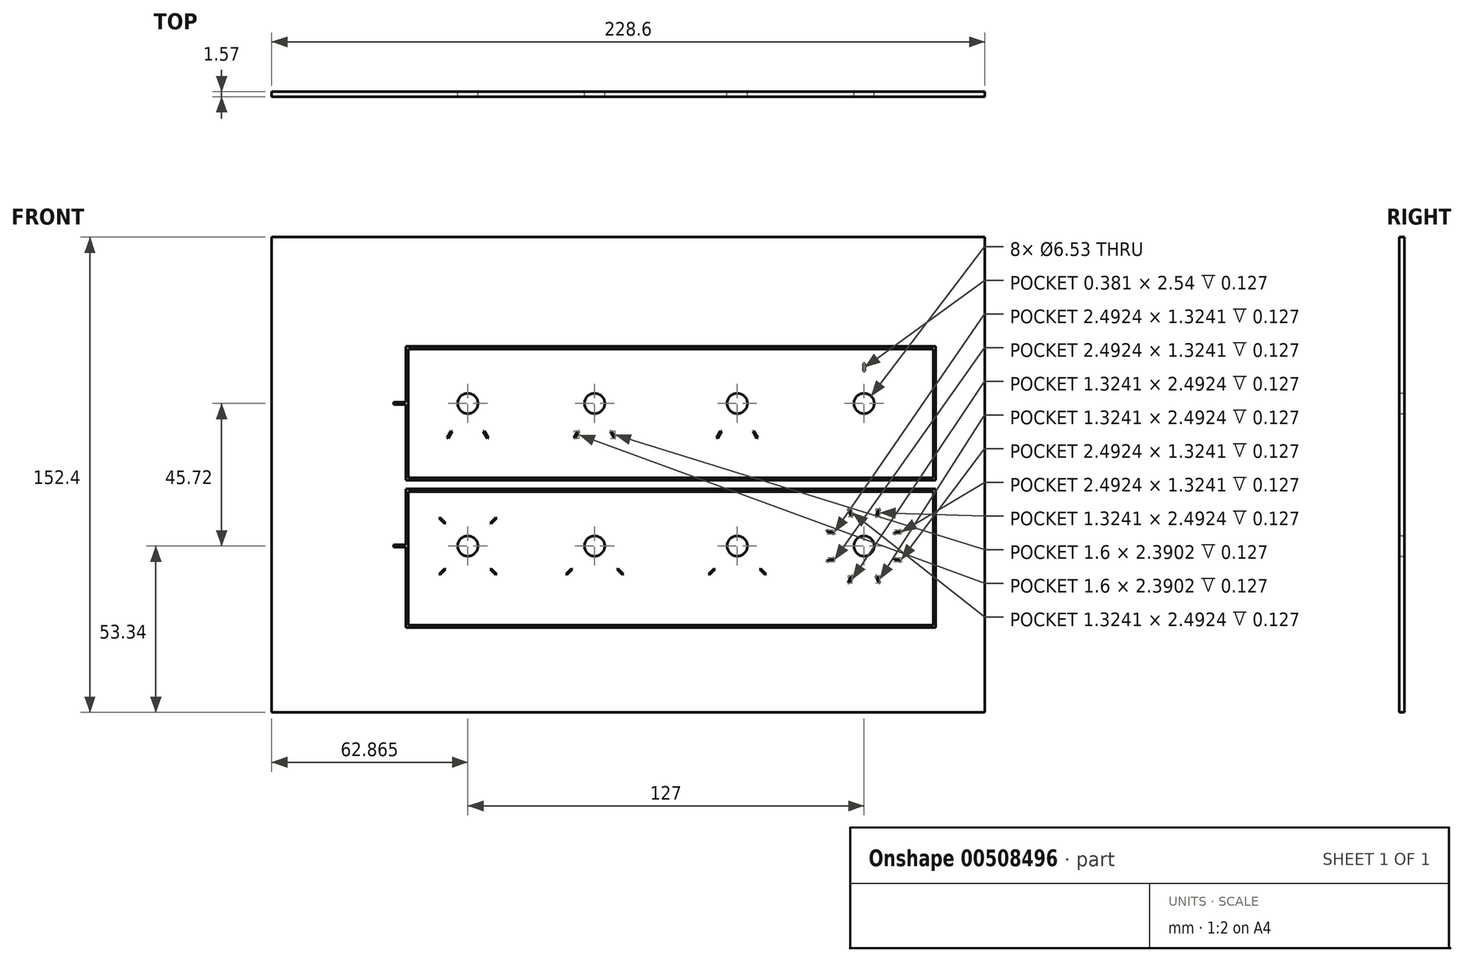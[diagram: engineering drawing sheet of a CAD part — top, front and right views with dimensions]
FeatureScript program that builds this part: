
annotation { "Feature Type Name" : "Feature", "Feature Type Description" : "" }
export const myFeature = defineFeature(function(context is Context, id is Id, definition is map)
    precondition{}
    {
        {
            var Q0;
            Q0=qCreatedBy(makeId("Front.planeOp"),FACE);
            var sketch = newSketch(context, id + "F0", { "sketchPlane" : qUnion([Q0])});
            skLineSegment(sketch, "E0.bottom", {"start": v(114.3, -76.2) * mm, "end": v(-114.3, -76.2) * mm});
            skLineSegment(sketch, "E0.top", {"start": v(114.3, 76.2) * mm, "end": v(-114.3, 76.2) * mm});
            skLineSegment(sketch, "E0.left", {"start": v(114.3, -76.2) * mm, "end": v(114.3, 76.2) * mm});
            skLineSegment(sketch, "E0.right", {"start": v(-114.3, -76.2) * mm, "end": v(-114.3, 76.2) * mm});
            skPoint(sketch, "E0.middle", {"position": v(0, 0) * mm});
            skSolve(sketch);
        }
        {
            var Q0;
            Q0=qSketchRegion(id+"F0",true);
            extrude(context, id + "F1", {"entities" : qUnion([Q0]), "depth" : 1.57 * mm});
        }
        {
            var Q0;
            Q0=makeQuery(id+"F1.opExtrude","CAP_FACE",FACE,{"disambiguationData":[OSD([sQuery(id+"F0.wireOp",EDGE,"E0.bottom"),sQuery(id+"F0.wireOp",EDGE,"E0.top"),sQuery(id+"F0.wireOp",EDGE,"E0.left"),sQuery(id+"F0.wireOp",EDGE,"E0.right")])],"isStart":false});
            var sketch = newSketch(context, id + "F2", { "sketchPlane" : qUnion([Q0])});
            skLineSegment(sketch, "E1", {"start": v(0, 117.54) * mm, "end": v(0, -147.27) * mm, "construction": true});
            skPoint(sketch, "E1.startSnap0", {"position": v(0, 76.2) * mm});
            skLineSegment(sketch, "E2", {"start": v(-154.79, 0) * mm, "end": v(171.18, 0) * mm, "construction": true});
            skPoint(sketch, "E2.endSnap0", {"position": v(114.3, 0) * mm});
            skLineSegment(sketch, "E3", {"start": v(-51.44, 120.6) * mm, "end": v(-51.43, -147.27) * mm, "construction": true});
            skLineSegment(sketch, "E4", {"start": v(-10.8, 117.54) * mm, "end": v(-10.8, -147.27) * mm, "construction": true});
            skLineSegment(sketch, "E5", {"start": v(34.93, 117.54) * mm, "end": v(34.93, -147.27) * mm, "construction": true});
            skLineSegment(sketch, "E6", {"start": v(75.57, 117.54) * mm, "end": v(75.57, -147.27) * mm, "construction": true});
            skLineSegment(sketch, "E7", {"start": v(-154.79, 22.86) * mm, "end": v(171.18, 22.86) * mm, "construction": true});
            skLineSegment(sketch, "E8", {"start": v(-154.79, -22.86) * mm, "end": v(171.18, -22.86) * mm, "construction": true});
            skPoint(sketch, "E9", {"position": v(-51.44, 22.86) * mm});
            skPoint(sketch, "E10", {"position": v(-10.8, 22.86) * mm});
            skPoint(sketch, "E11", {"position": v(34.93, 22.86) * mm});
            skPoint(sketch, "E12", {"position": v(75.57, 22.86) * mm});
            skPoint(sketch, "E13", {"position": v(75.57, -22.86) * mm});
            skPoint(sketch, "E14", {"position": v(34.93, -22.86) * mm});
            skPoint(sketch, "E15", {"position": v(-10.8, -22.86) * mm});
            skPoint(sketch, "E16", {"position": v(-51.43, -22.86) * mm});
            skSolve(sketch);
        }
        {
            var Q0;
            Q0=sQuery(id+"F2.wireOp",VERTEX,"E9");
            var Q1;
            Q1=sQuery(id+"F2.wireOp",VERTEX,"E10");
            var Q2;
            Q2=sQuery(id+"F2.wireOp",VERTEX,"E11");
            var Q3;
            Q3=sQuery(id+"F2.wireOp",VERTEX,"E12");
            var Q4;
            Q4=sQuery(id+"F2.wireOp",VERTEX,"E13");
            var Q5;
            Q5=sQuery(id+"F2.wireOp",VERTEX,"E14");
            var Q6;
            Q6=sQuery(id+"F2.wireOp",VERTEX,"E15");
            var Q7;
            Q7=sQuery(id+"F2.wireOp",VERTEX,"E16");
            var Q8;
            Q8=makeQuery(id+"F1.opExtrude","SWEPT_BODY",BODY,{"disambiguationData":[OSD([sQuery(id+"F0.wireOp",EDGE,"E0.bottom"),sQuery(id+"F0.wireOp",EDGE,"E0.top"),sQuery(id+"F0.wireOp",EDGE,"E0.left"),sQuery(id+"F0.wireOp",EDGE,"E0.right")])]});
            hole(context, id + "F3", {"style" : HoleStyle.SIMPLE, "endStyle" : HoleEndStyle.THROUGH, "holeDiameter" : 6.53 * mm, "tappedDepth" : 19.05 * mm, "tapClearance" : 3, "locations" : qUnion([Q0, Q1, Q2, Q3, Q4, Q5, Q6, Q7]), "scope" : qUnion([Q8]), "startStyle" : HoleStartStyle.PART});
        }
        {
            var Q0;
            Q0=makeQuery(id+"F1.opExtrude","CAP_FACE",FACE,{"disambiguationData":[OSD([sQuery(id+"F0.wireOp",EDGE,"E0.bottom"),sQuery(id+"F0.wireOp",EDGE,"E0.top"),sQuery(id+"F0.wireOp",EDGE,"E0.left"),sQuery(id+"F0.wireOp",EDGE,"E0.right")])],"isStart":false});
            var sketch = newSketch(context, id + "F4", { "sketchPlane" : qUnion([Q0])});
            skText(sketch, "E17", { "text": "Sweep", "fontName": "OpenSans-Regular.ttf"});
            skText(sketch, "E18", { "text": "Chan 1", "fontName": "OpenSans-Regular.ttf"});
            skLineSegment(sketch, "E19", {"start": v(-51.44, 22.86) * mm, "end": v(-51.43, -69.4) * mm, "construction": true});
            skLineSegment(sketch, "E20", {"start": v(-10.8, 22.86) * mm, "end": v(-10.8, -69.78) * mm, "construction": true});
            skLineSegment(sketch, "E21", {"start": v(34.93, 22.86) * mm, "end": v(34.93, -69.78) * mm, "construction": true});
            skLineSegment(sketch, "E22", {"start": v(75.57, 22.86) * mm, "end": v(75.57, -65.32) * mm, "construction": true});
            skText(sketch, "E23", { "text": "Chan 2", "fontName": "OpenSans-Regular.ttf"});
            skText(sketch, "E24", { "text": "Lissajous", "fontName": "OpenSans-Regular.ttf"});
            skText(sketch, "E25", { "text": "Retrace", "fontName": "OpenSans-Regular.ttf"});
            skText(sketch, "E26", { "text": "Range", "fontName": "OpenSans-Regular.ttf"});
            skText(sketch, "E27", { "text": "Center", "fontName": "OpenSans-Regular.ttf"});
            skText(sketch, "E28", { "text": "Rate", "fontName": "OpenSans-Regular.ttf"});
            skLineSegment(sketch, "E29", {"start": v(-51.43, -22.86) * mm, "end": v(-101.2, -22.86) * mm, "construction": true});
            skLineSegment(sketch, "E30", {"start": v(-51.44, 22.86) * mm, "end": v(-100.19, 22.86) * mm, "construction": true});
            skText(sketch, "E31", { "text": "Sweep", "fontName": "OpenSans-Regular.ttf"});
            skText(sketch, "E32", { "text": "Pattern", "fontName": "OpenSans-Regular.ttf"});
            const initialGuessF4  = {"E17": [-0.07303, -0.04488, 1, 0, 0.00447], "E18": [-0.03238, -0.04485, 1, 0, 0.00444], "E23": [0.01334, -0.04462, 1, 0, 0.00421], "E24": [0.05173, -0.0444, 1, 0, 0.00399], "E25": [-0.03268, 0.00132, 1, 0, 0.00399], "E26": [0.0148, 0.00132, 1, 0, 0.00399], "E27": [0.0547, 0.00132, 1, 0, 0.00399], "E28": [-0.06932, 0.00132, 1, 0, 0.00399], "E31": [-0.11598, 0.01968, 1, 0, 0.00635], "E32": [-0.11916, -0.02604, 1, 0, 0.00635]};
            skSetInitialGuess(sketch, initialGuessF4);
            skSolve(sketch);
        }
        {
            var Q0;
            {var subQ0=sQuery(id+"F0.wireOp",EDGE,"E0.left");var subQ1=sQuery(id+"F0.wireOp",EDGE,"E0.top");var subQ2=sQuery(id+"F0.wireOp",EDGE,"E0.bottom");var subQ3=sQuery(id+"F0.wireOp",EDGE,"E0.right");Q0=makeQuery(id+"F5hVuftEAmlaWp1_1.boolean.opBoolean","SPLIT",FACE,{"disambiguationData":[TD([makeQuery(id+"F1.opExtrude","SWEPT_FACE",FACE,{"disambiguationData":[OSD([subQ2])]})])],"derivedFrom":makeQuery(id+"F1.opExtrude","CAP_FACE",FACE,{"disambiguationData":[OSD([subQ2,subQ1,subQ0,subQ3])],"isStart":false})});}
            var sketch = newSketch(context, id + "F5", { "sketchPlane" : qUnion([Q0])});
            skCircle(sketch, "E33", {"center": v(-51.43, -22.86) * mm, "radius": 10.32 * mm, "construction": true});
            skCircle(sketch, "E34", {"center": v(-51.43, -22.86) * mm, "radius": 12.7 * mm, "construction": true});
            skLineSegment(sketch, "E35", {"start": v(-51.43, -22.86) * mm, "end": v(-41.93, -13.35) * mm, "construction": true});
            skLineSegment(sketch, "E36", {"start": v(-51.43, -22.86) * mm, "end": v(-41.87, -32.42) * mm, "construction": true});
            skLineSegment(sketch, "E37", {"start": v(-51.43, -22.86) * mm, "end": v(-51.43, -8.06) * mm, "construction": true});
            skLineSegment(sketch, "E38.bottom", {"start": v(-44, -30.02) * mm, "end": v(-42.2, -31.82) * mm});
            skLineSegment(sketch, "E38.top", {"start": v(-44.27, -30.29) * mm, "end": v(-42.48, -32.09) * mm});
            skLineSegment(sketch, "E38.left", {"start": v(-44, -30.02) * mm, "end": v(-44.27, -30.29) * mm});
            skLineSegment(sketch, "E38.right", {"start": v(-42.2, -31.82) * mm, "end": v(-42.48, -32.09) * mm});
            skLineSegment(sketch, "E39.bottom", {"start": v(-42.48, -13.63) * mm, "end": v(-44.27, -15.43) * mm});
            skLineSegment(sketch, "E39.top", {"start": v(-42.2, -13.9) * mm, "end": v(-44, -15.7) * mm});
            skLineSegment(sketch, "E39.left", {"start": v(-42.48, -13.63) * mm, "end": v(-42.2, -13.9) * mm});
            skLineSegment(sketch, "E39.right", {"start": v(-44.27, -15.43) * mm, "end": v(-44, -15.7) * mm});
            skCircle(sketch, "E40", {"center": v(75.57, -22.86) * mm, "radius": 10.32 * mm, "construction": true});
            skCircle(sketch, "E41", {"center": v(75.57, -22.86) * mm, "radius": 12.7 * mm, "construction": true});
            skLineSegment(sketch, "E42", {"start": v(75.57, -22.86) * mm, "end": v(75.57, 0) * mm, "construction": true});
            skLineSegment(sketch, "E43", {"start": v(75.57, -22.86) * mm, "end": v(84.9, -0.34) * mm, "construction": true});
            skLineSegment(sketch, "E44.1.0", {"start": v(75.57, -22.86) * mm, "end": v(66.24, -0.34) * mm, "construction": true});
            skLineSegment(sketch, "E44.2.0", {"start": v(75.57, -22.86) * mm, "end": v(53.05, -13.53) * mm, "construction": true});
            skLineSegment(sketch, "E44.3.0", {"start": v(75.57, -22.86) * mm, "end": v(53.05, -32.19) * mm, "construction": true});
            skLineSegment(sketch, "E44.4.0", {"start": v(75.57, -22.86) * mm, "end": v(66.24, -45.38) * mm, "construction": true});
            skLineSegment(sketch, "E44.5.0", {"start": v(75.57, -22.86) * mm, "end": v(84.9, -45.38) * mm, "construction": true});
            skLineSegment(sketch, "E44.6.0", {"start": v(75.57, -22.86) * mm, "end": v(98.08, -32.19) * mm, "construction": true});
            skLineSegment(sketch, "E44.7.0", {"start": v(75.57, -22.86) * mm, "end": v(98.08, -13.53) * mm, "construction": true});
            skLineSegment(sketch, "E45.bottom", {"start": v(79.34, -13.26) * mm, "end": v(80.3, -10.9) * mm});
            skLineSegment(sketch, "E45.top", {"start": v(79.69, -13.4) * mm, "end": v(80.66, -11.05) * mm});
            skLineSegment(sketch, "E45.left", {"start": v(79.34, -13.26) * mm, "end": v(79.69, -13.4) * mm});
            skLineSegment(sketch, "E45.right", {"start": v(80.3, -10.9) * mm, "end": v(80.66, -11.05) * mm});
            skLineSegment(sketch, "E46.1.0", {"start": v(85.17, -19.09) * mm, "end": v(87.52, -18.12) * mm});
            skLineSegment(sketch, "E46.1.1", {"start": v(85.02, -18.74) * mm, "end": v(87.37, -17.76) * mm});
            skLineSegment(sketch, "E46.1.2", {"start": v(87.37, -17.76) * mm, "end": v(87.52, -18.12) * mm});
            skLineSegment(sketch, "E46.1.3", {"start": v(85.02, -18.74) * mm, "end": v(85.17, -19.09) * mm});
            skLineSegment(sketch, "E46.2.0", {"start": v(85.02, -26.98) * mm, "end": v(87.37, -27.96) * mm});
            skLineSegment(sketch, "E46.2.1", {"start": v(85.17, -26.63) * mm, "end": v(87.52, -27.6) * mm});
            skLineSegment(sketch, "E46.2.2", {"start": v(87.52, -27.6) * mm, "end": v(87.37, -27.96) * mm});
            skLineSegment(sketch, "E46.2.3", {"start": v(85.17, -26.63) * mm, "end": v(85.02, -26.98) * mm});
            skLineSegment(sketch, "E46.3.0", {"start": v(79.34, -32.46) * mm, "end": v(80.3, -34.81) * mm});
            skLineSegment(sketch, "E46.3.1", {"start": v(79.69, -32.32) * mm, "end": v(80.66, -34.67) * mm});
            skLineSegment(sketch, "E46.3.2", {"start": v(80.66, -34.67) * mm, "end": v(80.3, -34.81) * mm});
            skLineSegment(sketch, "E46.3.3", {"start": v(79.69, -32.32) * mm, "end": v(79.34, -32.46) * mm});
            skLineSegment(sketch, "E46.4.0", {"start": v(71.44, -32.32) * mm, "end": v(70.47, -34.67) * mm});
            skLineSegment(sketch, "E46.4.1", {"start": v(71.8, -32.46) * mm, "end": v(70.82, -34.81) * mm});
            skLineSegment(sketch, "E46.4.2", {"start": v(70.82, -34.81) * mm, "end": v(70.47, -34.67) * mm});
            skLineSegment(sketch, "E46.4.3", {"start": v(71.8, -32.46) * mm, "end": v(71.44, -32.32) * mm});
            skLineSegment(sketch, "E46.5.0", {"start": v(65.96, -26.63) * mm, "end": v(63.61, -27.6) * mm});
            skLineSegment(sketch, "E46.5.1", {"start": v(66.1, -26.98) * mm, "end": v(63.76, -27.96) * mm});
            skLineSegment(sketch, "E46.5.2", {"start": v(63.76, -27.96) * mm, "end": v(63.61, -27.6) * mm});
            skLineSegment(sketch, "E46.5.3", {"start": v(66.1, -26.98) * mm, "end": v(65.96, -26.63) * mm});
            skLineSegment(sketch, "E46.6.0", {"start": v(66.1, -18.74) * mm, "end": v(63.76, -17.76) * mm});
            skLineSegment(sketch, "E46.6.1", {"start": v(65.96, -19.09) * mm, "end": v(63.61, -18.12) * mm});
            skLineSegment(sketch, "E46.6.2", {"start": v(63.61, -18.12) * mm, "end": v(63.76, -17.76) * mm});
            skLineSegment(sketch, "E46.6.3", {"start": v(65.96, -19.09) * mm, "end": v(66.1, -18.74) * mm});
            skLineSegment(sketch, "E46.7.0", {"start": v(71.8, -13.26) * mm, "end": v(70.82, -10.9) * mm});
            skLineSegment(sketch, "E46.7.1", {"start": v(71.44, -13.4) * mm, "end": v(70.47, -11.05) * mm});
            skLineSegment(sketch, "E46.7.2", {"start": v(70.47, -11.05) * mm, "end": v(70.82, -10.9) * mm});
            skLineSegment(sketch, "E46.7.3", {"start": v(71.44, -13.4) * mm, "end": v(71.8, -13.26) * mm});
            skLineSegment(sketch, "E46.anchor1", {"start": v(75.57, -22.86) * mm, "end": v(79.69, -13.4) * mm, "construction": true});
            skLineSegment(sketch, "E46.anchor2", {"start": v(75.57, -22.86) * mm, "end": v(71.8, -13.26) * mm, "construction": true});
            skLineSegment(sketch, "E47", {"start": v(-10.8, -22.86) * mm, "end": v(-10.8, -39.67) * mm, "construction": true});
            skLineSegment(sketch, "E48", {"start": v(34.93, -22.86) * mm, "end": v(34.93, -39.28) * mm, "construction": true});
            skCircle(sketch, "E49", {"center": v(-10.8, -22.86) * mm, "radius": 10.32 * mm, "construction": true});
            skCircle(sketch, "E50", {"center": v(-10.8, -22.86) * mm, "radius": 12.7 * mm, "construction": true});
            skCircle(sketch, "E51", {"center": v(34.93, -22.86) * mm, "radius": 10.32 * mm, "construction": true});
            skCircle(sketch, "E52", {"center": v(34.93, -22.86) * mm, "radius": 12.7 * mm, "construction": true});
            skLineSegment(sketch, "E53", {"start": v(-51.43, -22.86) * mm, "end": v(-65.5, -36.92) * mm, "construction": true});
            skLineSegment(sketch, "E54", {"start": v(-10.8, -22.86) * mm, "end": v(-24.75, -36.82) * mm, "construction": true});
            skLineSegment(sketch, "E55", {"start": v(-10.8, -22.86) * mm, "end": v(3.44, -37.1) * mm, "construction": true});
            skLineSegment(sketch, "E56", {"start": v(34.93, -22.86) * mm, "end": v(21.23, -36.55) * mm, "construction": true});
            skLineSegment(sketch, "E57", {"start": v(34.93, -22.86) * mm, "end": v(49.67, -37.6) * mm, "construction": true});
            skLineSegment(sketch, "E58.bottom", {"start": v(25.7, -31.82) * mm, "end": v(27.5, -30.02) * mm});
            skLineSegment(sketch, "E58.top", {"start": v(25.97, -32.09) * mm, "end": v(27.76, -30.29) * mm});
            skLineSegment(sketch, "E58.left", {"start": v(25.7, -31.82) * mm, "end": v(25.97, -32.09) * mm});
            skLineSegment(sketch, "E58.right", {"start": v(27.5, -30.02) * mm, "end": v(27.76, -30.29) * mm});
            skLineSegment(sketch, "E59.bottom", {"start": v(42.35, -30.02) * mm, "end": v(44.15, -31.82) * mm});
            skLineSegment(sketch, "E59.top", {"start": v(42.09, -30.29) * mm, "end": v(43.88, -32.09) * mm});
            skLineSegment(sketch, "E59.left", {"start": v(42.35, -30.02) * mm, "end": v(42.09, -30.29) * mm});
            skLineSegment(sketch, "E59.right", {"start": v(44.15, -31.82) * mm, "end": v(43.88, -32.09) * mm});
            skLineSegment(sketch, "E60.bottom", {"start": v(-20.02, -31.82) * mm, "end": v(-18.22, -30.02) * mm});
            skLineSegment(sketch, "E60.top", {"start": v(-19.75, -32.09) * mm, "end": v(-17.96, -30.29) * mm});
            skLineSegment(sketch, "E60.left", {"start": v(-20.02, -31.82) * mm, "end": v(-19.75, -32.09) * mm});
            skLineSegment(sketch, "E60.right", {"start": v(-18.22, -30.02) * mm, "end": v(-17.96, -30.29) * mm});
            skLineSegment(sketch, "E61.bottom", {"start": v(-3.37, -30.02) * mm, "end": v(-1.57, -31.82) * mm});
            skLineSegment(sketch, "E61.top", {"start": v(-3.63, -30.29) * mm, "end": v(-1.84, -32.09) * mm});
            skLineSegment(sketch, "E61.left", {"start": v(-3.37, -30.02) * mm, "end": v(-3.63, -30.29) * mm});
            skLineSegment(sketch, "E61.right", {"start": v(-1.57, -31.82) * mm, "end": v(-1.84, -32.09) * mm});
            skLineSegment(sketch, "E62.bottom", {"start": v(-60.66, -31.82) * mm, "end": v(-58.86, -30.02) * mm});
            skLineSegment(sketch, "E62.top", {"start": v(-60.4, -32.09) * mm, "end": v(-58.6, -30.29) * mm});
            skLineSegment(sketch, "E62.left", {"start": v(-60.66, -31.82) * mm, "end": v(-60.4, -32.09) * mm});
            skLineSegment(sketch, "E62.right", {"start": v(-58.86, -30.02) * mm, "end": v(-58.6, -30.29) * mm});
            skCircle(sketch, "E63", {"center": v(-51.44, 22.86) * mm, "radius": 10.32 * mm, "construction": true});
            skCircle(sketch, "E64", {"center": v(-51.44, 22.86) * mm, "radius": 12.7 * mm, "construction": true});
            skCircle(sketch, "E65", {"center": v(-10.8, 22.86) * mm, "radius": 10.32 * mm, "construction": true});
            skCircle(sketch, "E66", {"center": v(34.93, 22.86) * mm, "radius": 10.32 * mm, "construction": true});
            skCircle(sketch, "E67", {"center": v(75.57, 22.86) * mm, "radius": 10.32 * mm, "construction": true});
            skCircle(sketch, "E68", {"center": v(-10.8, 22.86) * mm, "radius": 12.7 * mm, "construction": true});
            skCircle(sketch, "E69", {"center": v(34.93, 22.86) * mm, "radius": 12.7 * mm, "construction": true});
            skCircle(sketch, "E70", {"center": v(75.57, 22.86) * mm, "radius": 12.7 * mm, "construction": true});
            skLineSegment(sketch, "E71", {"start": v(-10.8, 22.86) * mm, "end": v(-10.8, 0) * mm, "construction": true});
            skLineSegment(sketch, "E72", {"start": v(-10.8, 22.86) * mm, "end": v(-23.44, 0.97) * mm, "construction": true});
            skLineSegment(sketch, "E73", {"start": v(-10.8, 22.86) * mm, "end": v(2.14, 0.45) * mm, "construction": true});
            skLineSegment(sketch, "E74.bottom", {"start": v(-17.39, 11.82) * mm, "end": v(-16.12, 14.02) * mm});
            skLineSegment(sketch, "E74.top", {"start": v(-17.06, 11.63) * mm, "end": v(-15.79, 13.83) * mm});
            skLineSegment(sketch, "E74.left", {"start": v(-17.39, 11.82) * mm, "end": v(-17.06, 11.63) * mm});
            skLineSegment(sketch, "E74.right", {"start": v(-16.12, 14.02) * mm, "end": v(-15.79, 13.83) * mm});
            skLineSegment(sketch, "E75.bottom", {"start": v(-5.47, 14.02) * mm, "end": v(-4.2, 11.82) * mm});
            skLineSegment(sketch, "E75.top", {"start": v(-5.8, 13.83) * mm, "end": v(-4.53, 11.63) * mm});
            skLineSegment(sketch, "E75.left", {"start": v(-5.47, 14.02) * mm, "end": v(-5.8, 13.83) * mm});
            skLineSegment(sketch, "E75.right", {"start": v(-4.2, 11.82) * mm, "end": v(-4.53, 11.63) * mm});
            skLineSegment(sketch, "E76", {"start": v(-51.43, 22.86) * mm, "end": v(-51.43, 6.58) * mm, "construction": true});
            skLineSegment(sketch, "E77", {"start": v(-51.44, 22.86) * mm, "end": v(-60.83, 6.58) * mm, "construction": true});
            skLineSegment(sketch, "E78", {"start": v(-51.44, 22.86) * mm, "end": v(-42.04, 6.58) * mm, "construction": true});
            skLineSegment(sketch, "E79.bottom", {"start": v(-58.03, 11.82) * mm, "end": v(-56.76, 14.02) * mm});
            skLineSegment(sketch, "E79.top", {"start": v(-57.7, 11.63) * mm, "end": v(-56.43, 13.83) * mm});
            skLineSegment(sketch, "E79.left", {"start": v(-58.03, 11.82) * mm, "end": v(-57.7, 11.63) * mm});
            skLineSegment(sketch, "E79.right", {"start": v(-56.76, 14.02) * mm, "end": v(-56.43, 13.83) * mm});
            skLineSegment(sketch, "E80.bottom", {"start": v(-46.11, 14.02) * mm, "end": v(-44.84, 11.82) * mm});
            skLineSegment(sketch, "E80.top", {"start": v(-46.44, 13.83) * mm, "end": v(-45.17, 11.63) * mm});
            skLineSegment(sketch, "E80.left", {"start": v(-46.11, 14.02) * mm, "end": v(-46.44, 13.83) * mm});
            skLineSegment(sketch, "E80.right", {"start": v(-44.84, 11.82) * mm, "end": v(-45.17, 11.63) * mm});
            skLineSegment(sketch, "E81", {"start": v(75.57, 22.86) * mm, "end": v(75.57, 41.9) * mm, "construction": true});
            skLineSegment(sketch, "E82.bottom", {"start": v(75.37, 35.72) * mm, "end": v(75.76, 35.72) * mm});
            skLineSegment(sketch, "E82.top", {"start": v(75.37, 33.18) * mm, "end": v(75.76, 33.18) * mm});
            skLineSegment(sketch, "E82.left", {"start": v(75.37, 35.72) * mm, "end": v(75.37, 33.18) * mm});
            skLineSegment(sketch, "E82.right", {"start": v(75.76, 35.72) * mm, "end": v(75.76, 33.18) * mm});
            skLineSegment(sketch, "E83", {"start": v(34.93, 22.86) * mm, "end": v(34.93, 3.94) * mm, "construction": true});
            skLineSegment(sketch, "E84", {"start": v(34.92, 22.86) * mm, "end": v(24, 3.94) * mm, "construction": true});
            skLineSegment(sketch, "E85", {"start": v(34.93, 22.86) * mm, "end": v(45.85, 3.94) * mm});
            skLineSegment(sketch, "E86.bottom", {"start": v(28.33, 11.82) * mm, "end": v(29.6, 14.02) * mm});
            skLineSegment(sketch, "E86.top", {"start": v(28.66, 11.63) * mm, "end": v(29.93, 13.83) * mm});
            skLineSegment(sketch, "E86.left", {"start": v(28.33, 11.82) * mm, "end": v(28.66, 11.63) * mm});
            skLineSegment(sketch, "E86.right", {"start": v(29.6, 14.02) * mm, "end": v(29.93, 13.83) * mm});
            skLineSegment(sketch, "E87.bottom", {"start": v(40.25, 14.02) * mm, "end": v(41.52, 11.82) * mm});
            skLineSegment(sketch, "E87.top", {"start": v(39.92, 13.83) * mm, "end": v(41.19, 11.63) * mm});
            skLineSegment(sketch, "E87.left", {"start": v(40.25, 14.02) * mm, "end": v(39.92, 13.83) * mm});
            skLineSegment(sketch, "E87.right", {"start": v(41.52, 11.82) * mm, "end": v(41.19, 11.63) * mm});
            skLineSegment(sketch, "E88", {"start": v(-51.43, -22.86) * mm, "end": v(-63.42, -10.87) * mm, "construction": true});
            skLineSegment(sketch, "E89.bottom", {"start": v(-60.4, -13.63) * mm, "end": v(-58.6, -15.43) * mm});
            skLineSegment(sketch, "E89.top", {"start": v(-60.66, -13.9) * mm, "end": v(-58.86, -15.7) * mm});
            skLineSegment(sketch, "E89.left", {"start": v(-60.4, -13.63) * mm, "end": v(-60.66, -13.9) * mm});
            skLineSegment(sketch, "E89.right", {"start": v(-58.6, -15.43) * mm, "end": v(-58.86, -15.7) * mm});
            skSolve(sketch);
        }
        {
            var Q0;
            Q0=qSketchRegion(id+"F5",true);
            extrude(context, id + "F6", {"entities" : qUnion([Q0]), "operationType" : NewBodyOperationType.REMOVE, "oppositeDirection" : true, "depth" : 0.13 * mm, "offsetDistance" : 25.4 * mm});
        }
        {
            var Q0;
            {var subQ0=sQuery(id+"F0.wireOp",EDGE,"E0.left");var subQ1=sQuery(id+"F0.wireOp",EDGE,"E0.bottom");var subQ2=sQuery(id+"F0.wireOp",EDGE,"E0.right");var subQ3=sQuery(id+"F0.wireOp",EDGE,"E0.top");Q0=makeQuery(id+"F5hVuftEAmlaWp1_1.boolean.opBoolean","SPLIT",FACE,{"disambiguationData":[TD([makeQuery(id+"F1.opExtrude","SWEPT_FACE",FACE,{"disambiguationData":[OSD([subQ1])]})])],"derivedFrom":makeQuery(id+"F1.opExtrude","CAP_FACE",FACE,{"disambiguationData":[OSD([subQ1,subQ3,subQ0,subQ2])],"isStart":false})});}
            var sketch = newSketch(context, id + "F7", { "sketchPlane" : qUnion([Q0])});
            skLineSegment(sketch, "E90.bottom", {"start": v(-70.48, 40.32) * mm, "end": v(97.8, 40.32) * mm});
            skLineSegment(sketch, "E90.top", {"start": v(-70.48, -0.95) * mm, "end": v(97.8, -0.95) * mm});
            skLineSegment(sketch, "E90.left", {"start": v(-70.48, 40.32) * mm, "end": v(-70.48, -0.95) * mm});
            skLineSegment(sketch, "E90.right", {"start": v(97.8, 40.32) * mm, "end": v(97.8, -0.95) * mm});
            skLineSegment(sketch, "E91.bottom", {"start": v(-70.48, -5.4) * mm, "end": v(97.8, -5.4) * mm});
            skLineSegment(sketch, "E91.top", {"start": v(-70.48, -48.26) * mm, "end": v(97.8, -48.26) * mm});
            skLineSegment(sketch, "E91.left", {"start": v(-70.48, -5.4) * mm, "end": v(-70.48, -48.26) * mm});
            skLineSegment(sketch, "E91.right", {"start": v(97.8, -5.4) * mm, "end": v(97.8, -48.26) * mm});
            skLineSegment(sketch, "E92", {"start": v(-51.44, 22.86) * mm, "end": v(-51.43, -22.86) * mm, "construction": true});
            skLineSegment(sketch, "E93", {"start": v(75.57, 22.86) * mm, "end": v(75.57, -22.86) * mm, "construction": true});
            skLineSegment(sketch, "E94", {"start": v(-51.43, -22.86) * mm, "end": v(-116, -22.86) * mm, "construction": true});
            skLineSegment(sketch, "E95.0", {"start": v(-71.28, 41.12) * mm, "end": v(98.58, 41.12) * mm});
            skLineSegment(sketch, "E95.1", {"start": v(-71.28, 41.12) * mm, "end": v(-71.28, -1.75) * mm});
            skLineSegment(sketch, "E95.2", {"start": v(-71.28, -1.75) * mm, "end": v(98.58, -1.75) * mm});
            skLineSegment(sketch, "E95.3", {"start": v(98.58, 41.12) * mm, "end": v(98.58, -1.75) * mm});
            skLineSegment(sketch, "E96.0", {"start": v(-71.28, -4.6) * mm, "end": v(98.58, -4.6) * mm});
            skLineSegment(sketch, "E96.1", {"start": v(-71.28, -4.6) * mm, "end": v(-71.28, -49.05) * mm});
            skLineSegment(sketch, "E96.2", {"start": v(-71.28, -49.05) * mm, "end": v(98.58, -49.05) * mm});
            skLineSegment(sketch, "E96.3", {"start": v(98.58, -4.6) * mm, "end": v(98.58, -49.05) * mm});
            skLineSegment(sketch, "E97.bottom", {"start": v(-75.25, 23.26) * mm, "end": v(-71.28, 23.26) * mm});
            skLineSegment(sketch, "E97.top", {"start": v(-75.25, 22.46) * mm, "end": v(-71.28, 22.46) * mm});
            skLineSegment(sketch, "E97.left", {"start": v(-75.25, 23.26) * mm, "end": v(-75.25, 22.46) * mm});
            skLineSegment(sketch, "E97.right", {"start": v(-71.28, 23.26) * mm, "end": v(-71.28, 22.46) * mm});
            skLineSegment(sketch, "E98.bottom", {"start": v(-75.25, -22.46) * mm, "end": v(-71.28, -22.46) * mm});
            skLineSegment(sketch, "E98.top", {"start": v(-75.25, -23.26) * mm, "end": v(-71.28, -23.26) * mm});
            skLineSegment(sketch, "E98.left", {"start": v(-75.25, -22.46) * mm, "end": v(-75.25, -23.26) * mm});
            skLineSegment(sketch, "E98.right", {"start": v(-71.28, -22.46) * mm, "end": v(-71.28, -23.26) * mm});
            skLineSegment(sketch, "E99", {"start": v(-51.44, 22.86) * mm, "end": v(-112.61, 22.86) * mm, "construction": true});
            skSolve(sketch);
        }
        {
            var Q0;
            Q0=makeQuery(id+"F7.imprint","IMPRINT",FACE,{"disambiguationData":[TD([[makeQuery(id+"F7.imprint","IMPRINT",EDGE,{"derivedFrom":sQuery(id+"F7.wireOp",EDGE,"E90.bottom")}),1.0]])]});
            var Q1;
            Q1=makeQuery(id+"F7.imprint","IMPRINT",FACE,{"disambiguationData":[TD([[makeQuery(id+"F7.imprint","IMPRINT",EDGE,{"derivedFrom":sQuery(id+"F7.wireOp",EDGE,"E97.bottom")}),-1.0]])]});
            var Q2;
            Q2=makeQuery(id+"F7.imprint","IMPRINT",FACE,{"disambiguationData":[TD([[makeQuery(id+"F7.imprint","IMPRINT",EDGE,{"derivedFrom":sQuery(id+"F7.wireOp",EDGE,"E91.bottom")}),1.0]])]});
            var Q3;
            Q3=makeQuery(id+"F7.imprint","IMPRINT",FACE,{"disambiguationData":[TD([[makeQuery(id+"F7.imprint","IMPRINT",EDGE,{"derivedFrom":sQuery(id+"F7.wireOp",EDGE,"E98.bottom")}),-1.0]])]});
            extrude(context, id + "F8", {"entities" : qUnion([Q0, Q1, Q2, Q3]), "operationType" : NewBodyOperationType.REMOVE, "oppositeDirection" : true, "depth" : 0.13 * mm, "offsetDistance" : 25.4 * mm});
        }
    });
